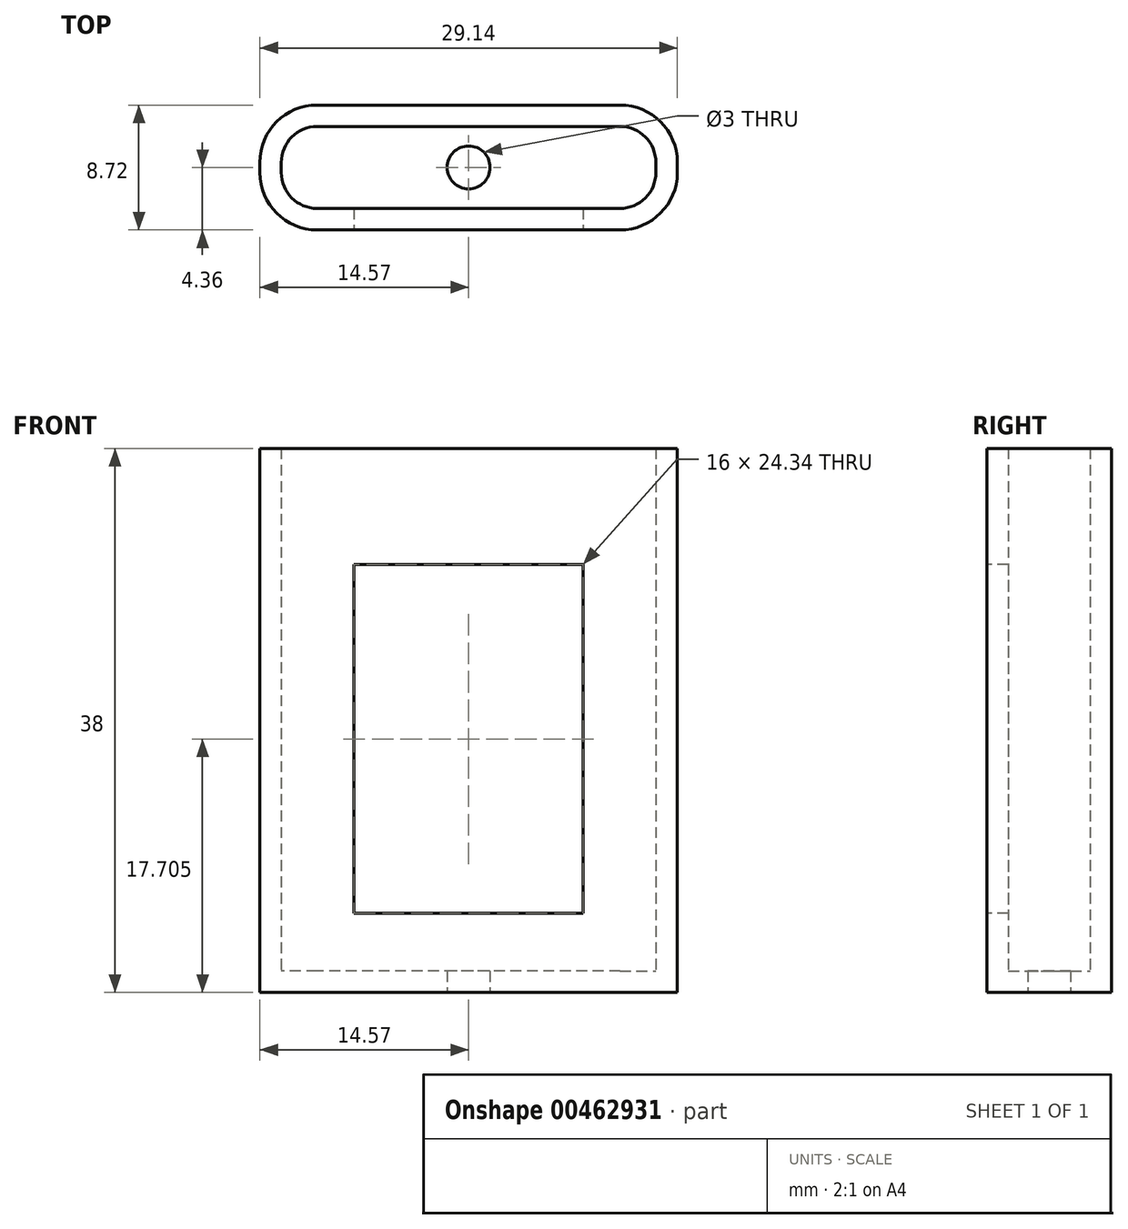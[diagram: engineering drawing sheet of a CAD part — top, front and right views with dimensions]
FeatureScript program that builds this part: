
annotation { "Feature Type Name" : "Feature", "Feature Type Description" : "" }
export const myFeature = defineFeature(function(context is Context, id is Id, definition is map)
    precondition{}
    {
        {
            var Q0;
            Q0=qCreatedBy(makeId("Top.planeOp"),FACE);
            var sketch = newSketch(context, id + "F0", { "sketchPlane" : qUnion([Q0])});
            skLineSegment(sketch, "E0.bottom", {"start": v(10.57, 4.36) * mm, "end": v(-10.57, 4.36) * mm});
            skLineSegment(sketch, "E0.top", {"start": v(10.57, -4.36) * mm, "end": v(-10.57, -4.36) * mm});
            skLineSegment(sketch, "E0.left", {"start": v(14.57, 0.36) * mm, "end": v(14.57, -0.36) * mm});
            skLineSegment(sketch, "E0.right", {"start": v(-14.57, 0.36) * mm, "end": v(-14.57, -0.36) * mm});
            skPoint(sketch, "E0.middle", {"position": v(0, 0) * mm});
            skPoint(sketch, "E1.visualSharp", {"position": v(14.57, 4.36) * mm});
            skArc(sketch, "E1.filletArc", {"start": v(14.57, 0.36) * mm, "mid": v(13.4, 3.19) * mm, "end": v(10.57, 4.36) * mm});
            skPoint(sketch, "E2.visualSharp", {"position": v(14.57, -4.36) * mm});
            skArc(sketch, "E2.filletArc", {"start": v(10.57, -4.36) * mm, "mid": v(13.4, -3.19) * mm, "end": v(14.57, -0.36) * mm});
            skPoint(sketch, "E3.visualSharp", {"position": v(-14.57, -4.36) * mm});
            skArc(sketch, "E3.filletArc", {"start": v(-14.57, -0.36) * mm, "mid": v(-13.4, -3.19) * mm, "end": v(-10.57, -4.36) * mm});
            skPoint(sketch, "E4.visualSharp", {"position": v(-14.57, 4.36) * mm});
            skArc(sketch, "E4.filletArc", {"start": v(-10.57, 4.36) * mm, "mid": v(-13.4, 3.19) * mm, "end": v(-14.57, 0.36) * mm});
            skSolve(sketch);
        }
        {
            var Q0;
            Q0=makeQuery(id+"F0.imprint","IMPRINT",FACE,{"disambiguationData":[TD([[makeQuery(id+"F0.imprint","IMPRINT",EDGE,{"derivedFrom":sQuery(id+"F0.wireOp",EDGE,"E0.bottom")}),1.0]])]});
            extrude(context, id + "F1", {"entities" : qUnion([Q0]), "depth" : 38 * mm});
        }
        {
            var Q0;
            Q0=makeQuery(id+"F1.opExtrude","CAP_FACE",FACE,{"disambiguationData":[OSD([sQuery(id+"F0.wireOp",EDGE,"E0.bottom"),sQuery(id+"F0.wireOp",EDGE,"E0.top"),sQuery(id+"F0.wireOp",EDGE,"E0.left"),sQuery(id+"F0.wireOp",EDGE,"E0.right"),sQuery(id+"F0.wireOp",EDGE,"E1.filletArc"),sQuery(id+"F0.wireOp",EDGE,"E2.filletArc"),sQuery(id+"F0.wireOp",EDGE,"E3.filletArc"),sQuery(id+"F0.wireOp",EDGE,"E4.filletArc")])],"isStart":false});
            shell(context, id + "F2", {"entities" : qUnion([Q0]), "thickness" : 1.5 * mm});
        }
        {
            var Q0;
            Q0=qCreatedBy(makeId("Top.planeOp"),FACE);
            var sketch = newSketch(context, id + "F3", { "sketchPlane" : qUnion([Q0])});
            skCircle(sketch, "E5", {"center": v(0, 0) * mm, "radius": 1.5 * mm});
            skSolve(sketch);
        }
        {
            var Q0;
            Q0=makeQuery(id+"F3.imprint","IMPRINT",FACE,{"disambiguationData":[TD([[makeQuery(id+"F3.imprint","IMPRINT",EDGE,{"derivedFrom":sQuery(id+"F3.wireOp",EDGE,"E5")}),1.0]])]});
            extrude(context, id + "F4", {"entities" : qUnion([Q0]), "operationType" : NewBodyOperationType.REMOVE, "depth" : 25 * mm});
        }
        {
            var Q0;
            Q0=makeQuery(id+"F1.opExtrude","SWEPT_FACE",FACE,{"disambiguationData":[OSD([sQuery(id+"F0.wireOp",EDGE,"E0.top")])]});
            var sketch = newSketch(context, id + "F5", { "sketchPlane" : qUnion([Q0])});
            skLineSegment(sketch, "E6.bottom", {"start": v(8, 29.87) * mm, "end": v(-8, 29.87) * mm});
            skLineSegment(sketch, "E6.top", {"start": v(8, 5.54) * mm, "end": v(-8, 5.54) * mm});
            skLineSegment(sketch, "E6.left", {"start": v(8, 29.87) * mm, "end": v(8, 5.54) * mm});
            skLineSegment(sketch, "E6.right", {"start": v(-8, 29.87) * mm, "end": v(-8, 5.54) * mm});
            skPoint(sketch, "E6.middle", {"position": v(0, 17.7) * mm});
            skSolve(sketch);
        }
        {
            var Q0;
            Q0=makeQuery(id+"F5.imprint","IMPRINT",FACE,{"disambiguationData":[TD([[makeQuery(id+"F5.imprint","IMPRINT",EDGE,{"derivedFrom":sQuery(id+"F5.wireOp",EDGE,"E6.bottom")}),1.0]])]});
            extrude(context, id + "F6", {"entities" : qUnion([Q0]), "operationType" : NewBodyOperationType.REMOVE, "oppositeDirection" : true, "depth" : 3 * mm});
        }
    });
